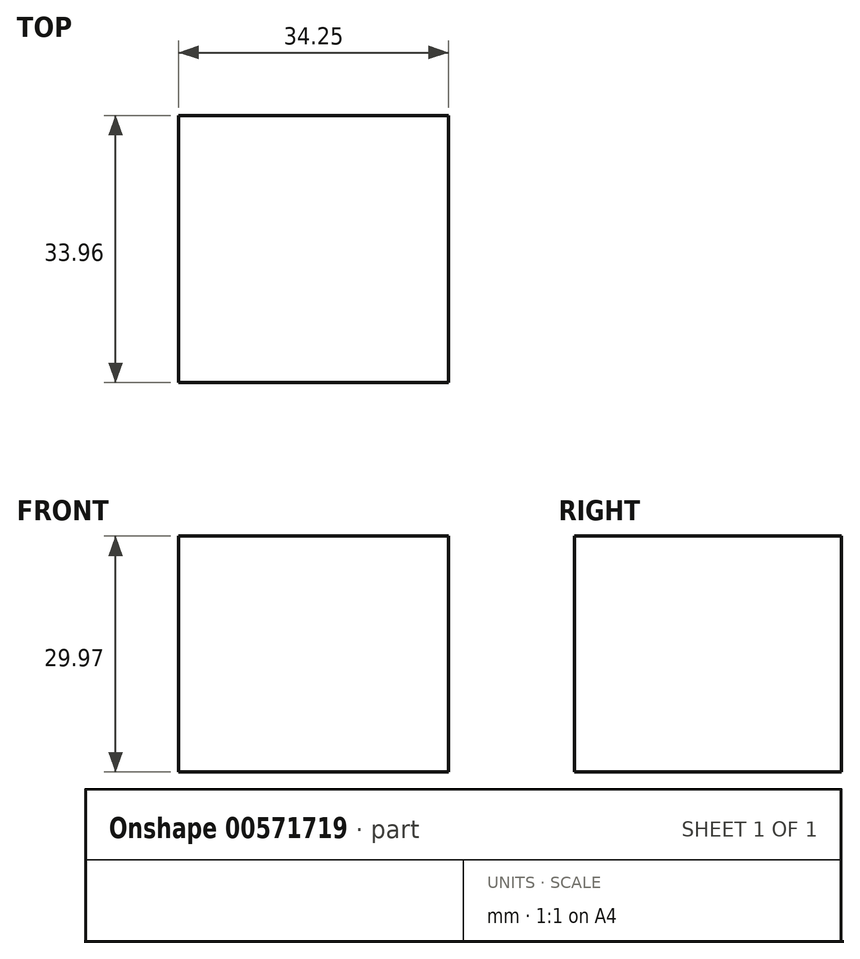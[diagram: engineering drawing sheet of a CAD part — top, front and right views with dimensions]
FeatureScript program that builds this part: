
annotation { "Feature Type Name" : "Feature", "Feature Type Description" : "" }
export const myFeature = defineFeature(function(context is Context, id is Id, definition is map)
    precondition{}
    {
        {
            var Q0;
            Q0=qCreatedBy(makeId("Top.planeOp"),FACE);
            var sketch = newSketch(context, id + "F0", { "sketchPlane" : qUnion([Q0])});
            skLineSegment(sketch, "E0.bottom", {"start": v(-57.56, 58.42) * mm, "end": v(-23.31, 58.42) * mm});
            skLineSegment(sketch, "E0.top", {"start": v(-57.56, 24.46) * mm, "end": v(-23.31, 24.46) * mm});
            skLineSegment(sketch, "E0.left", {"start": v(-57.56, 58.42) * mm, "end": v(-57.56, 24.46) * mm});
            skLineSegment(sketch, "E0.right", {"start": v(-23.31, 58.42) * mm, "end": v(-23.31, 24.46) * mm});
            skSolve(sketch);
        }
        {
            var Q0;
            Q0=makeQuery(id+"F0.imprint","IMPRINT",FACE,{"disambiguationData":[TD([[makeQuery(id+"F0.imprint","IMPRINT",EDGE,{"derivedFrom":sQuery(id+"F0.wireOp",EDGE,"E0.bottom")}),-1.0]])]});
            extrude(context, id + "F1", {"entities" : qUnion([Q0]), "depth" : 29.97 * mm, "offsetDistance" : 25.4 * mm});
        }
    });
